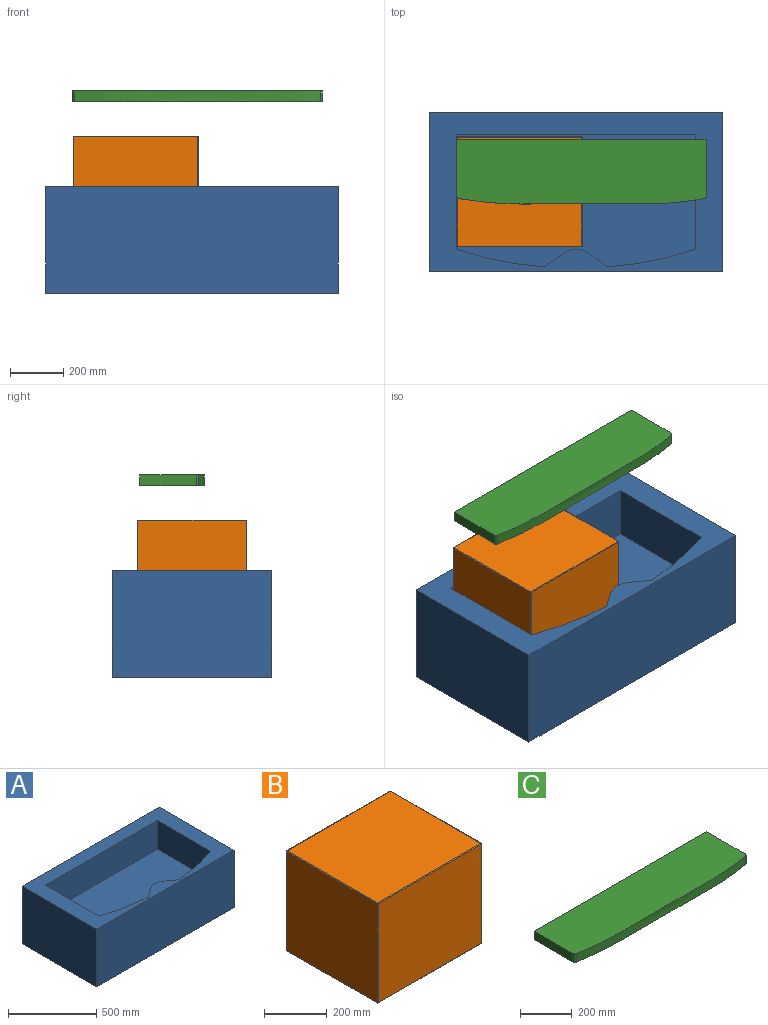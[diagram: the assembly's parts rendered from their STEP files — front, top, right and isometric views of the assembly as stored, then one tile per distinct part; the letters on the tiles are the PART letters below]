
ASSEMBLY  parts=3 mates=2
PART A: 13 faces, bbox 1100x600x400 mm
  f0: plane 600x400mm, normal (-1,0,0), area 240000mm2, adj f1,f3,f4,f5
  f1: plane 1100x400mm, normal (0,-1,0), area 440000mm2, adj f0,f2,f4,f5
  f2: plane 600x400mm, normal (1,0,0), area 240000mm2, adj f1,f3,f4,f5
  f3: plane 1100x400mm, normal (0,1,0), area 440000mm2, adj f0,f2,f4,f5
  f4: plane 1100x600mm, normal (0,0,1), area 239495.4mm2, adj f0,f1,f2,f3,f6,f7,f8,f9
  f5: plane 1100x600mm, normal (0,0,-1), area 660000mm2, adj f0,f1,f2,f3
  f6: extruded ~240x200mm, area 55648.7mm2, adj f4,f7,f11,f12
  f7: extruded ~330x200mm, area 67531.8mm2, adj f4,f6,f8,f12
  f8: plane 430x200mm, normal (-1,0,0), area 86000mm2, adj f4,f7,f9,f12
  f9: plane 900x200mm, normal (0,-1,0), area 180000mm2, adj f4,f8,f10,f12
  f10: plane 430x200mm, normal (1,0,0), area 86000mm2, adj f4,f9,f11,f12
  f11: extruded ~330x200mm, area 67531.8mm2, adj f4,f6,f10,f12
  f12: plane 900x499.41mm, normal (0,0,1), area 420504.6mm2, adj f6,f7,f8,f9,f10,f11
PART B: 26 faces, bbox 470x412x390 mm
  f0: plane 466x386mm, normal (0,1,0), area 179876mm2, adj f14,f19,f22,f25
  f1: plane 408x386mm, normal (-1,0,0), area 157488mm2, adj f11,f20,f21,f25
  f2: plane 466x386mm, normal (0,-1,0), area 179876mm2, adj f6,f10,f11,f12
  f3: plane 408x386mm, normal (1,0,0), area 157488mm2, adj f6,f9,f13,f14
  f4: plane 466x408mm, normal (0,0,1), area 190128mm2, adj f9,f10,f19,f20
  f5: plane 466x408mm, normal (0,0,-1), area 190128mm2, adj f12,f13,f21,f22
  f6: cylinder r=2mm len=386mm, axis (0,0,-1), area 1212.7mm2, adj f2,f3,f7,f8
  f7: sphere r=2mm, area 6.3mm2, adj f6,f9,f10
  f8: sphere r=2mm, area 6.3mm2, adj f6,f12,f13
  f9: cylinder r=2mm len=408mm, axis (0,-1,0), area 1281.8mm2, adj f3,f4,f7,f15
  f10: cylinder r=2mm len=466mm, axis (-1,0,0), area 1464mm2, adj f2,f4,f7,f16
  f11: cylinder r=2mm len=386mm, axis (0,0,1), area 1212.7mm2, adj f1,f2,f16,f17
  f12: cylinder r=2mm len=466mm, axis (1,0,0), area 1464mm2, adj f2,f5,f8,f17
  f13: cylinder r=2mm len=408mm, axis (0,1,0), area 1281.8mm2, adj f3,f5,f8,f18
  f14: cylinder r=2mm len=386mm, axis (0,0,1), area 1212.7mm2, adj f0,f3,f15,f18
  f15: sphere r=2mm, area 6.3mm2, adj f9,f14,f19
  f16: sphere r=2mm, area 6.3mm2, adj f10,f11,f20
  f17: sphere r=2mm, area 6.3mm2, adj f11,f12,f21
  f18: sphere r=2mm, area 6.3mm2, adj f13,f14,f22
  f19: cylinder r=2mm len=466mm, axis (1,0,0), area 1464mm2, adj f0,f4,f15,f23
  f20: cylinder r=2mm len=408mm, axis (0,1,0), area 1281.8mm2, adj f1,f4,f16,f23
  f21: cylinder r=2mm len=408mm, axis (0,-1,0), area 1281.8mm2, adj f1,f5,f17,f24
  f22: cylinder r=2mm len=466mm, axis (-1,0,0), area 1464mm2, adj f0,f5,f18,f24
  f23: sphere r=2mm, area 6.3mm2, adj f19,f20,f25
  f24: sphere r=2mm, area 6.3mm2, adj f21,f22,f25
  f25: cylinder r=2mm len=386mm, axis (0,0,-1), area 1212.7mm2, adj f0,f1,f23,f24
PART C: 13 faces, bbox 940x246.1x40 mm
  f0: plane 940x246.13mm, normal (0,0,-1), area 36469.9mm2, adj f1,f2,f3,f4,f5,f6,f8,f9
  f1: cylinder r=10mm len=40mm, axis (0,0,-1), area 551.4mm2, adj f0,f2,f6,f7
  f2: extruded ~923.82x40mm, area 37052.1mm2, adj f0,f1,f3,f7
  f3: cylinder r=10mm len=40mm, axis (0,0,-1), area 551.4mm2, adj f0,f2,f4,f7
  f4: plane 211.8x40mm, normal (1,0,0), area 8471.9mm2, adj f0,f3,f5,f7
  f5: plane 940x40mm, normal (0,1,0), area 37600mm2, adj f0,f4,f6,f7
  f6: plane 211.8x40mm, normal (-1,0,0), area 8471.9mm2, adj f0,f1,f5,f7
  f7: plane 940x246.13mm, normal (0,0,1), area 223689mm2, adj f1,f2,f3,f4,f5,f6
  f8: extruded ~907.55x30mm, area 27234.1mm2, adj f0,f9,f11,f12
  f9: plane 199.52x30mm, normal (1,0,0), area 5985.7mm2, adj f0,f8,f10,f12
  f10: plane 913.29x30mm, normal (0,-1,0), area 27398.8mm2, adj f0,f9,f11,f12
  f11: plane 199.52x30mm, normal (-1,0.03,0), area 5988.2mm2, adj f0,f8,f10,f12
  f12: plane 913.29x209.88mm, normal (0,0,-1), area 187219.1mm2, adj f8,f9,f10,f11
PLACE A t=(-58.89,72.15,-40.77)mm fixed
PLACE B t=(-505.89,-133.85,159.23)mm
PLACE C t=(-38.89,158.05,679.23)mm
MATE slider C.f7 <-> A.f4  axis (0,0,1) through (-508.89,162.15,719.23)mm
MATE fastened A.f12 <-> B.f5  axis (0,0,1) through (-508.89,72.15,159.23)mm
